# Revit family: Shower-Shower_Door-KOHLER-Levity_Plus-K-702421_1
name_source: partatom
category: Specialty Equipment
units: mm (PartAtom-declared; Revit-internal decimal feet)

## family parameters
Cut with Voids When Loaded = No
Host = Face
Maintain Annotation Orientation = No
OmniClass Number = 23.31.17.17
OmniClass Title = Shower Enclosures
Part Type = Normal
Room Calculation Point = No
Round Connector Dimension = Use Diameter
Shared = No

## types (4) — shared parameters
ADA Compliant = No
Assembly Code = C1030200
Date Modified = 03/17/2022
Default Elevation = 4"
Description = 5/16 SHOWER DOOR 78 X 47-5/8 HANDLE
Height = 77 9/16"
Length = 6 15/16"
Manufacturer = KOHLER Co.
Master Format 2014 = 10 28 19.16
Master Format 2014 Name = Shower Doors
Material = Premium Metal Construction
Product Documentation Link = https://www.us.kohler.com
Product Name = Levity Plus
Product Page URL = http://www.us.kohler.com
URL = https://www.us.kohler.com
WaterSense Certified = No

## per-type parameters (varying)
| type | Finish | Model | Type |
| SHP-Bright Polished Silver | Kohler-Metal-SHP-Bright_Polished_Silver | K-702421-L-SHP | 1 |
| BNK-Anodized Brushed Nickel | Kohler-Metal-BNK-Anodized_Brushed_Nickel | K-702421-L-BNK | 2 |
| BL-Matte Black | Kohler-Metal-BL-Matte_Black | K-702421-L-BL | 3 |
| 2MB-Vibrant Brushed Moderne Brass | Kohler-Metal-2MB-Vibrant_Brushed_Moderne_Brass | K-702421-L-2MB | 4 |

## geometry (parser evidence)
native form markers: Sweep x6
no freeform markers — native parametric forms only
